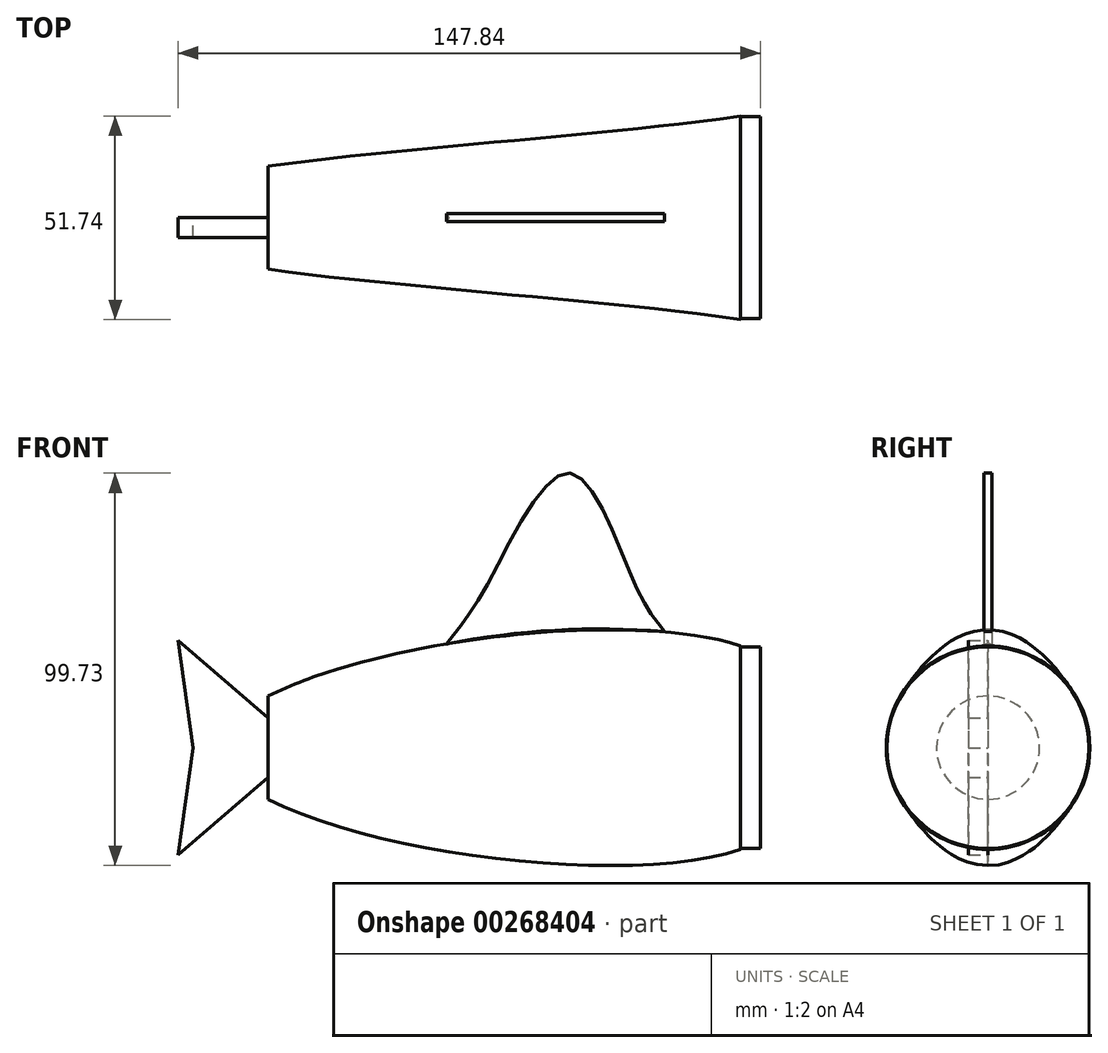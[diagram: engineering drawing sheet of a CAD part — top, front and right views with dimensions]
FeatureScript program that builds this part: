
annotation { "Feature Type Name" : "Feature", "Feature Type Description" : "" }
export const myFeature = defineFeature(function(context is Context, id is Id, definition is map)
    precondition{}
    {
        {
            var Q0;
            Q0=qCreatedBy(makeId("Right.planeOp"),FACE);
            cPlane(context, id + "F0", {"entities" : qUnion([Q0]), "cplaneType" : CPlaneType.OFFSET, "offset" : 120 * mm, "oppositeDirection" : true, "width" : 150 * mm, "height" : 150 * mm});
        }
        {
            var Q0;
            Q0=qCreatedBy(id+"F0.planeOp",FACE);
            var sketch = newSketch(context, id + "F1", { "sketchPlane" : qUnion([Q0])});
            skCircle(sketch, "E0", {"center": v(0, 0) * mm, "radius": 13.1 * mm});
            skSolve(sketch);
        }
        {
            var Q0;
            Q0=qCreatedBy(makeId("Right.planeOp"),FACE);
            var sketch = newSketch(context, id + "F2", { "sketchPlane" : qUnion([Q0])});
            skCircle(sketch, "E1", {"center": v(0, 0) * mm, "radius": 25.87 * mm});
            skSolve(sketch);
        }
        {
            var Q0;
            Q0=qCreatedBy(makeId("Top.planeOp"),FACE);
            var sketch = newSketch(context, id + "F3", { "sketchPlane" : qUnion([Q0])});
            skLineSegment(sketch, "E2.0", {"start": v(-120, 13.1) * mm, "end": v(-120, -13.1) * mm});
            skLineSegment(sketch, "E3.0", {"start": v(0, 25.87) * mm, "end": v(0, -25.87) * mm});
            skFitSpline(sketch, "E4", {"points": [v(-120, 13.1) * mm, v(0, 25.87) * mm], "startDerivative": vector(93.86, -24.3) * mm, "endDerivative": vector(85.47, 2.62) * mm});
            skFitSpline(sketch, "E5", {"points": [v(-120, -13.1) * mm, v(0, -25.87) * mm], "startDerivative": vector(93.86, 24.3) * mm, "endDerivative": vector(85.79, -2.62) * mm});
            skSolve(sketch);
        }
        {
            var Q0;
            Q0=qCreatedBy(makeId("Front.planeOp"),FACE);
            var sketch = newSketch(context, id + "F4", { "sketchPlane" : qUnion([Q0])});
            skLineSegment(sketch, "E6.0", {"start": v(-120, 13.1) * mm, "end": v(-120, -13.1) * mm});
            skLineSegment(sketch, "E7.0", {"start": v(0, 25.87) * mm, "end": v(0, -25.87) * mm});
            skFitSpline(sketch, "E8", {"points": [v(-120, 13.1) * mm, v(0, 25.87) * mm], "startDerivative": vector(88.32, 44.7) * mm, "endDerivative": vector(81.79, -27.38) * mm});
            skFitSpline(sketch, "E9.MirrorCS", {"points": [v(-120, -13.1) * mm, v(0, -25.87) * mm], "startDerivative": vector(88.32, -44.7) * mm, "endDerivative": vector(81.79, 27.38) * mm});
            skSolve(sketch);
        }
        {
            var Q0;
            Q0=makeQuery(id+"F2.imprint","IMPRINT",FACE,{"disambiguationData":[TD([[makeQuery(id+"F2.imprint","IMPRINT",EDGE,{"derivedFrom":sQuery(id+"F2.wireOp",EDGE,"E1")}),1.0]])]});
            var Q1;
            Q1=makeQuery(id+"F1.imprint","IMPRINT",FACE,{"disambiguationData":[TD([[makeQuery(id+"F1.imprint","IMPRINT",EDGE,{"derivedFrom":sQuery(id+"F1.wireOp",EDGE,"E0")}),1.0]])]});
            var Q2;
            Q2=sQuery(id+"F4.wireOp",EDGE,"E9.MirrorCS");
            var Q3;
            Q3=sQuery(id+"F4.wireOp",EDGE,"E8");
            loft(context, id + "F5", {"addGuides" : true, "sheetProfilesArray" : [{ "sheetProfileEntities" : qUnion([Q0]) }, { "sheetProfileEntities" : qUnion([Q1]) }], "guidesArray" : [{ "guideEntities" : qUnion([Q2]), "guideDerivativeType" : LoftGuideDerivativeType.DEFAULT, "guideDerivativeMagnitude" : 1 }, { "guideEntities" : qUnion([Q3]), "guideDerivativeType" : LoftGuideDerivativeType.DEFAULT, "guideDerivativeMagnitude" : 1 }]});
        }
        {
            var Q0;
            Q0=makeQuery(id+"F5.opLoft","CAP_FACE",FACE,{"disambiguationData":[OSD([makeQuery(id+"F2.imprint","IMPRINT",FACE,{"disambiguationData":[TD([[makeQuery(id+"F2.imprint","IMPRINT",EDGE,{"derivedFrom":sQuery(id+"F2.wireOp",EDGE,"E1")}),1.0]])]})])],"isStart":true});
            var sketch = newSketch(context, id + "F6", { "sketchPlane" : qUnion([Q0])});
            skCircle(sketch, "E10", {"center": v(0, 0) * mm, "radius": 25.64 * mm});
            skSolve(sketch);
        }
        {
            var Q0;
            Q0 = qSketchRegion(id + "F6", true);
            extrude(context, id + "F7", {"entities" : qUnion([Q0]), "operationType" : NewBodyOperationType.ADD, "depth" : 5 * mm});
        }
        {
            var Q0;
            Q0=qCreatedBy(makeId("Front.planeOp"),FACE);
            var sketch = newSketch(context, id + "F8", { "sketchPlane" : qUnion([Q0])});
            skLineSegment(sketch, "E11", {"start": v(-120, 7.57) * mm, "end": v(-142.84, 27.3) * mm});
            skLineSegment(sketch, "E12", {"start": v(-142.84, 27.3) * mm, "end": v(-139.12, 0) * mm});
            skLineSegment(sketch, "E13", {"start": v(-20.21, 0) * mm, "end": v(-157.42, 0) * mm, "construction": true});
            skLineSegment(sketch, "E14.MirrorCS", {"start": v(-142.84, -27.3) * mm, "end": v(-139.12, 0) * mm});
            skLineSegment(sketch, "E15.MirrorCS", {"start": v(-120, -7.57) * mm, "end": v(-142.84, -27.3) * mm});
            skArc(sketch, "E16", {"start": v(-120, -7.57) * mm, "mid": v(-119.75, 0) * mm, "end": v(-120, 7.57) * mm});
            skSolve(sketch);
        }
        {
            var Q0;
            Q0=makeQuery(id+"F8.imprint","IMPRINT",FACE,{"disambiguationData":[TD([[makeQuery(id+"F8.imprint","IMPRINT",EDGE,{"derivedFrom":sQuery(id+"F8.wireOp",EDGE,"E11")}),1.0]])]});
            extrude(context, id + "F9", {"entities" : qUnion([Q0]), "operationType" : NewBodyOperationType.ADD, "depth" : 5 * mm});
        }
        {
            var Q0;
            Q0=qCreatedBy(makeId("Front.planeOp"),FACE);
            var sketch = newSketch(context, id + "F10", { "sketchPlane" : qUnion([Q0])});
            skFitSpline(sketch, "E17", {"points": [v(-19.3, 29.4) * mm, v(-43.92, 55.88) * mm, v(-74.75, 26.34) * mm], "startDerivative": vector(-49.99, 81.52) * mm, "endDerivative": vector(-60.19, -88) * mm});
            skSolve(sketch);
        }
        {
            var Q0;
            Q0=qCreatedBy(makeId("Front.planeOp"),FACE);
            var sketch = newSketch(context, id + "F11", { "sketchPlane" : qUnion([Q0])});
            skArc(sketch, "E18", {"start": v(-19.1, 29.5) * mm, "mid": v(-47.03, 29.84) * mm, "end": v(-74.75, 26.34) * mm});
            skPoint(sketch, "E19.0", {"position": v(-74.75, 26.34) * mm});
            skFitSpline(sketch, "E20.0", {"points": [v(-19.3, 29.4) * mm, v(-27.28, 42.42) * mm, v(-43.59, 69.76) * mm, v(-64.3, 41.61) * mm, v(-74.75, 26.34) * mm]});
            skSolve(sketch);
        }
        {
            var Q0;
            Q0 = qSketchRegion(id + "F11", true);
            var Q1;
            Q1 = qSketchRegion(id + "F10", true);
            extrude(context, id + "F12", {"entities" : qUnion([Q0, Q1]), "operationType" : NewBodyOperationType.ADD, "endBound" : BoundingType.SYMMETRIC, "depth" : 2 * mm});
        }
    });
